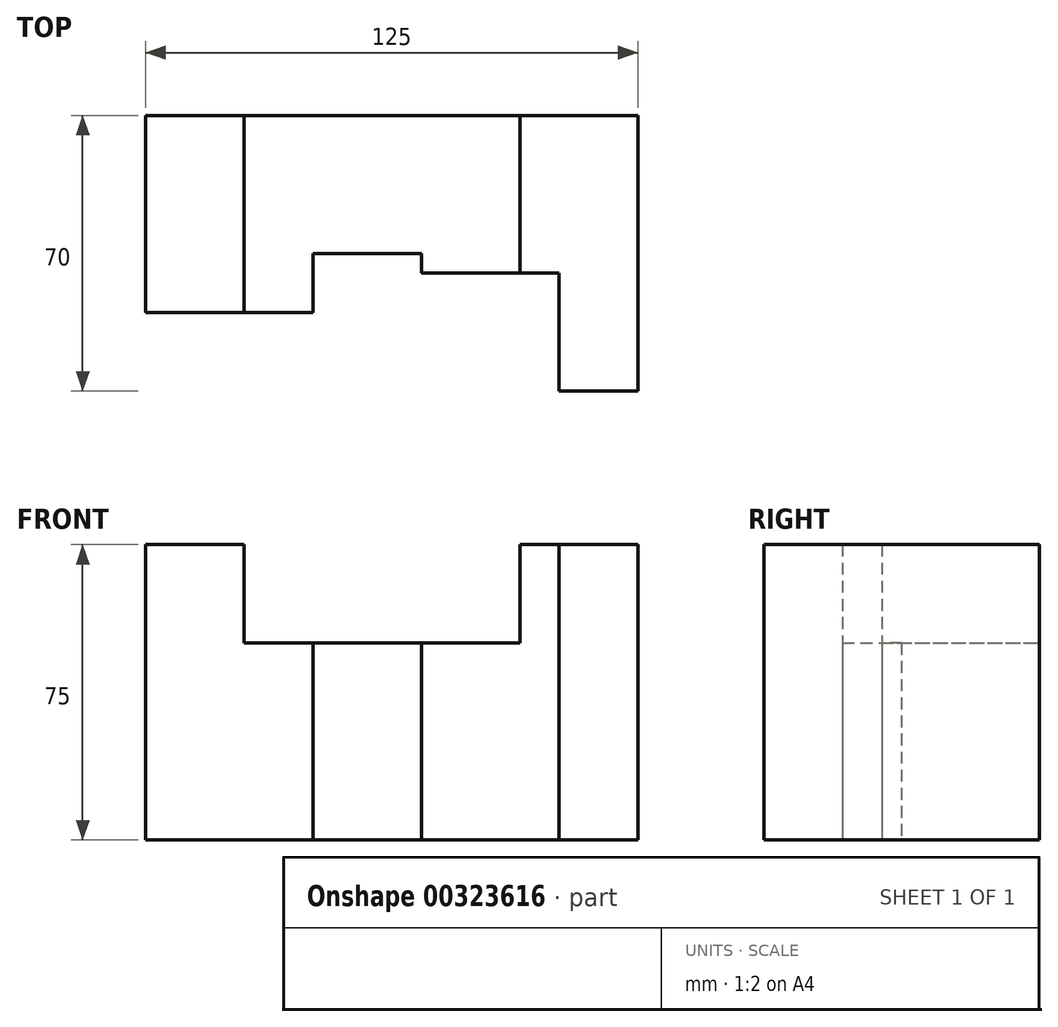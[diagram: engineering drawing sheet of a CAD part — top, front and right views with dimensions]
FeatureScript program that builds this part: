
annotation { "Feature Type Name" : "Feature", "Feature Type Description" : "" }
export const myFeature = defineFeature(function(context is Context, id is Id, definition is map)
    precondition{}
    {
        {
            var Q0;
            Q0=qCreatedBy(makeId("Top.planeOp"),FACE);
            var sketch = newSketch(context, id + "F0", { "sketchPlane" : qUnion([Q0])});
            skLineSegment(sketch, "E0", {"start": v(0, 0) * mm, "end": v(0, 50) * mm});
            skLineSegment(sketch, "E1", {"start": v(0, 50) * mm, "end": v(25, 50) * mm});
            skLineSegment(sketch, "E2", {"start": v(25, 50) * mm, "end": v(25, 0) * mm, "construction": true});
            skLineSegment(sketch, "E3", {"start": v(0, 0) * mm, "end": v(25, 0) * mm});
            skLineSegment(sketch, "E4", {"start": v(25, 0) * mm, "end": v(42.5, 0) * mm});
            skLineSegment(sketch, "E5", {"start": v(42.5, 0) * mm, "end": v(42.5, 15) * mm});
            skLineSegment(sketch, "E6", {"start": v(42.5, 15) * mm, "end": v(45, 15) * mm});
            skLineSegment(sketch, "E7", {"start": v(45, 15) * mm, "end": v(70, 15) * mm});
            skLineSegment(sketch, "E8", {"start": v(70, 15) * mm, "end": v(70, 10) * mm});
            skLineSegment(sketch, "E9", {"start": v(70, 10) * mm, "end": v(105, 10) * mm});
            skLineSegment(sketch, "E10", {"start": v(105, 10) * mm, "end": v(105, -20) * mm});
            skLineSegment(sketch, "E11", {"start": v(105, -20) * mm, "end": v(125, -20) * mm});
            skLineSegment(sketch, "E12", {"start": v(125, -20) * mm, "end": v(125, 50) * mm});
            skPoint(sketch, "E12.endSnap0", {"position": v(12.5, 50) * mm});
            skLineSegment(sketch, "E13", {"start": v(125, 50) * mm, "end": v(25, 50) * mm});
            skSolve(sketch);
        }
        {
            var Q0;
            Q0=qSketchRegion(id+"F0",true);
            extrude(context, id + "F1", {"entities" : qUnion([Q0]), "depth" : 50 * mm});
        }
        {
            var Q0;
            Q0=makeQuery(id+"F1.opExtrude","CAP_FACE",FACE,{"disambiguationData":[OSD([sQuery(id+"F0.wireOp",EDGE,"E0"),sQuery(id+"F0.wireOp",EDGE,"E1"),sQuery(id+"F0.wireOp",EDGE,"E3"),sQuery(id+"F0.wireOp",EDGE,"E4"),sQuery(id+"F0.wireOp",EDGE,"E5"),sQuery(id+"F0.wireOp",EDGE,"E6"),sQuery(id+"F0.wireOp",EDGE,"E7"),sQuery(id+"F0.wireOp",EDGE,"E8"),sQuery(id+"F0.wireOp",EDGE,"E9"),sQuery(id+"F0.wireOp",EDGE,"E10"),sQuery(id+"F0.wireOp",EDGE,"E11"),sQuery(id+"F0.wireOp",EDGE,"E12"),sQuery(id+"F0.wireOp",EDGE,"E13")])],"isStart":false});
            var sketch = newSketch(context, id + "F2", { "sketchPlane" : qUnion([Q0])});
            skLineSegment(sketch, "E14", {"start": v(0, 0) * mm, "end": v(25, 0) * mm});
            skLineSegment(sketch, "E15", {"start": v(25, 0) * mm, "end": v(25, 50) * mm});
            skLineSegment(sketch, "E16", {"start": v(25, 50) * mm, "end": v(0, 50) * mm});
            skLineSegment(sketch, "E17", {"start": v(0, 50) * mm, "end": v(0, 0) * mm});
            skLineSegment(sketch, "E18", {"start": v(125, 50) * mm, "end": v(125, -20) * mm});
            skLineSegment(sketch, "E19", {"start": v(125, -20) * mm, "end": v(105, -20) * mm});
            skLineSegment(sketch, "E20", {"start": v(105, -20) * mm, "end": v(105, 10) * mm});
            skLineSegment(sketch, "E21", {"start": v(105, 10) * mm, "end": v(95, 10) * mm});
            skLineSegment(sketch, "E22", {"start": v(95, 10) * mm, "end": v(95, 50) * mm});
            skLineSegment(sketch, "E23", {"start": v(95, 50) * mm, "end": v(125, 50) * mm});
            skSolve(sketch);
        }
        {
            var Q0;
            Q0=qSketchRegion(id+"F2",true);
            extrude(context, id + "F3", {"entities" : qUnion([Q0]), "operationType" : NewBodyOperationType.ADD, "depth" : 25 * mm});
        }
    });
